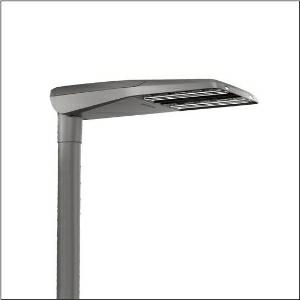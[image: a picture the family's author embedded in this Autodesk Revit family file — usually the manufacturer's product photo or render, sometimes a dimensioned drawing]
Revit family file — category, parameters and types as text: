
# Revit family: streetlight_sl_11_iq_midi___st1_0a_5xc3m51f08me_eb90
name_source: partatom
category: Lighting Fixtures
units: mm (PartAtom-declared; Revit-internal decimal feet)

## family parameters
Cut with Voids When Loaded = No
Host = Face
Light Source = No
Part Type = Normal
Room Calculation Point = No
Round Connector Dimension = Use Diameter
Shared = No

## types (1)
- --- (1 x LED, 17550 lm, 124.7 W, 3000K)
    Apparent Load = 125 VA
    CIE Flux Codes = 33 66 96 100 100
    Color Rendering = 70
    Color Temperature = 3000K
    Default Elevation = 1800 mm
    Description = Streetlight SL 11 iQ midi, mast luminaire, primary light control with 3 zone facetted reflector, of plastic, silver coated, highly specular, primary optical cover: cover, of PMMA, transparent, light distribution: ST1.0a, light emission: direct distribution, primary light characteristic: asymmetric, installation type: post-top, side-entry, lamps: LED, High Power LED, rated values: 17.550lm | 124,7W | 140,7lm/W (begin service life); end service life: 17.550lm | 132,2W; at 50% lumin. flux: 8.775lm | 57,2W | 153,4lm/W, colour temperature: 3000K, colour rendering: CRI > 70, light colour: 730, light setting 1 begin service life: 100% | 17.550lm | 124,7W | 140,7lm/W | 3.000K, light setting 1 end service life: 132,2W, further light settings possible, control: optimised constant luminous flux control (CLO 2.0), Street-Remote, Desk-Remote (wireless, voltage-free reading and setting of iQ features in the workshop via application-optimized NFC function/RFID function), Light-Fading, Smart-Wire, Night-Set, Lumen-Switch, Temp-Guard, Auto-Match, with cable H07RN-F 3x 1.5mm², mains connection: 230..240V, AC, 50/60Hz, connection cable pre-assembled, cable length: 12,5m, luminaire housing, of diecast aluminium, powder-coated, SITECO metallic grey (DB 702S), please order mast flange separately, inclination adjustable without tools: 0°, 5°, 10°, 15° (post-top) | 0°, -5°, -10°, -15° (side-entry), sealing non-destructively replaceable, multi-level sealing system, length: 780mm, width: 376mm, height: 118mm, mast flange for spigot size: 42mm (side-entry): 5XC10008XM4, 60/48mm (side-entry/post-top): 5XC10108XM2, 76/60mm (side-entry/post-top): 5XC10108XM1, equipment: Power, protection rating (complete): IP66, insulation class (complete): insulation class II (safety insulation), certification: CE, ENEC, ENEC+, VDE, impact resistance: IK10, permissible operating ambient temperature for outdoor applications: -25..+50°C, standard-compliant lighting for roads and squares, Environmental Product Declaration (EPD) tested and certified by an independent institute, packaging unit: 1 piece

Light Distribution: ST1.0a
    Height = 118 mm
    Lamp = 1 x LED
    Lamp Light Flux = 17550 lm
    Lamp Power = 124.7 W
    Lamp count = 1
    Length = 780 mm
    Luminous efficacy = 141 lm/W
    Manufacturer = Siteco
    ModVariant = No
    Model = 5XC3M51F08ME
    Number of Poles = 1
    OnlyDefault = Yes
    Power Factor = 1
    Product Name = Streetlight SL 11 iQ midi | ST1.0a
    Product group = mast luminaire | pylon top
    ProductGroupID = 6100
    Protection Class = Protection class II
    Protection Degree = IP 66
    RLX_Detail_Level = 1
    RLX_Emergency_Light_Flux = 0 lm
    RLX_Emergency_Type = 0
    RLX_Emergency_Type_DB = No
    RlxData = <blob elided: 70373 chars, md5=f836f7a6>
    Socket = socket
    Standby Power = 0 W
    System Light Flux = 17550 lm
    System Power = 125 W
    Type Comments = factory setting: luminous flux: 100 % | dim-lin: 254 | 557 mA
    Type Image = l_1005960.jpg
    URL = http://relux.com
    VarID = @adj_092341
    Voltage = 0 V
    Weight = 0.00 kg
    Width = 376 mm

## geometry (parser evidence)
native form markers: Blend x4, Sweep x10
no freeform markers — native parametric forms only
